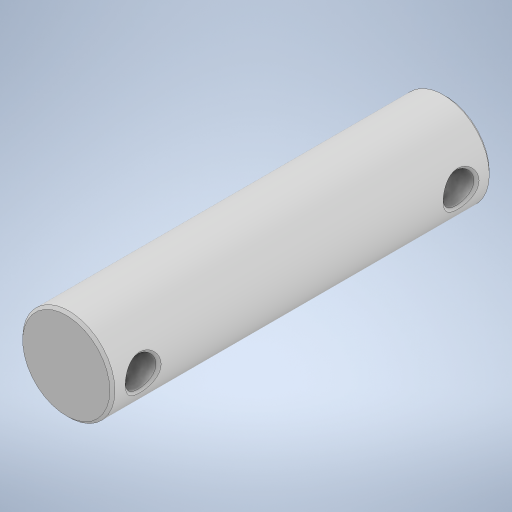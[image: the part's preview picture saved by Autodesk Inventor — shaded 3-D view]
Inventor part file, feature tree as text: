
AUTODESK INVENTOR PART (.ipt)
format: ipt  version: 2023 (Build 270158000, 158)  size: 274,432 bytes
history: native  units: mm
features: other x6, sketch x2, extrude x1, hole x1, chamfer x1
ambient origin geometry x8: Origin, YZ Plane, XZ Plane, XY Plane, X Axis, Y Axis, Z Axis, Center Point
bodies: Solido1 (feature_tree)
feature tree (11):
  other  "Tabella"
  other  "05-16-2023 Perno-01"
  other  "05-16-2023 Perno-02"
  other  "05-16-2023 Perno-03"
  other  "05-16-2023 Perno-04"
  other  "05-16-2023 Perno-05"
  extrude  "Estrusione1"  TaperAngle=0.0deg  [1 undecoded]
  hole  "Foro1"  [1 undecoded]
  chamfer  "Smusso1"  [1 undecoded]
  sketch  "Schizzo1"
  sketch  "Schizzo2"
note: 3 required parameter values undecoded (feature->parameter linkage not recoverable at this tier; creation-order binding heuristic only, values carry confidence <= 0.55)
